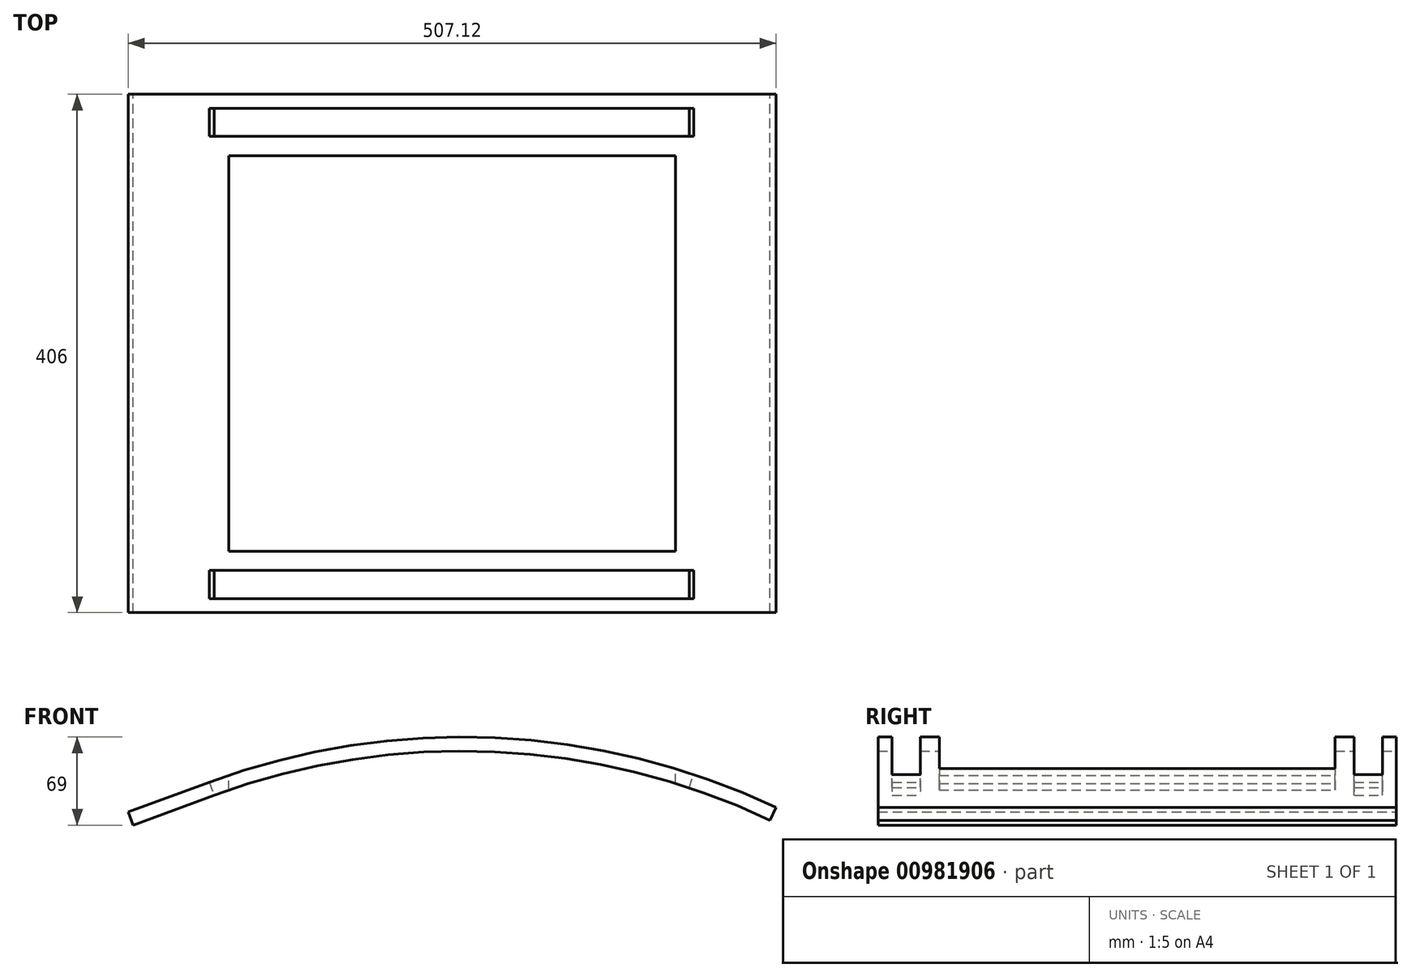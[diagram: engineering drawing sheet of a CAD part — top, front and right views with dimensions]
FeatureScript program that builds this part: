
annotation { "Feature Type Name" : "Feature", "Feature Type Description" : "" }
export const myFeature = defineFeature(function(context is Context, id is Id, definition is map)
    precondition{}
    {
        {
            var Q0;
            Q0=qCreatedBy(makeId("Front.planeOp"),FACE);
            var sketch = newSketch(context, id + "F0", { "sketchPlane" : qUnion([Q0])});
            skArc(sketch, "E0", {"start": v(249.02, -30.69) * mm, "mid": v(33.29, 22.94) * mm, "end": v(-186.38, -11.17) * mm});
            skArc(sketch, "E1", {"start": v(253.56, -20.66) * mm, "mid": v(33.68, 33.93) * mm, "end": v(-190.19, -0.84) * mm});
            skLineSegment(sketch, "E2", {"start": v(-249.76, -34.5) * mm, "end": v(-186.38, -11.17) * mm});
            skLineSegment(sketch, "E3", {"start": v(-253.56, -24.18) * mm, "end": v(-190.19, -0.84) * mm});
            skLineSegment(sketch, "E4", {"start": v(-249.76, -34.5) * mm, "end": v(-253.56, -24.18) * mm});
            skLineSegment(sketch, "E5", {"start": v(253.56, -20.66) * mm, "end": v(249.02, -30.69) * mm});
            skSolve(sketch);
        }
        {
            var Q0;
            Q0=makeQuery(id+"F0.imprint","IMPRINT",FACE,{"disambiguationData":[TD([[makeQuery(id+"F0.imprint","IMPRINT",EDGE,{"derivedFrom":sQuery(id+"F0.wireOp",EDGE,"E0")}),-1.0]])]});
            extrude(context, id + "F1", {"entities" : qUnion([Q0]), "depth" : 406 * mm, "offsetDistance" : 25 * mm});
        }
        {
            var Q0;
            Q0=makeQuery(id+"F1.opExtrude","CAP_FACE",FACE,{"disambiguationData":[OSD([sQuery(id+"F0.wireOp",EDGE,"E0"),sQuery(id+"F0.wireOp",EDGE,"E1"),sQuery(id+"F0.wireOp",EDGE,"E2"),sQuery(id+"F0.wireOp",EDGE,"E3"),sQuery(id+"F0.wireOp",EDGE,"E4"),sQuery(id+"F0.wireOp",EDGE,"E5")])],"isStart":false});
            cPlane(context, id + "F2", {"entities" : qUnion([Q0]), "cplaneType" : CPlaneType.OFFSET, "offset" : 11 * mm, "oppositeDirection" : true, "width" : 150 * mm, "height" : 150 * mm});
        }
        {
            var Q0;
            Q0=qCreatedBy(id+"F2.planeOp",FACE);
            var sketch = newSketch(context, id + "F3", { "sketchPlane" : qUnion([Q0])});
            skArc(sketch, "E6.0", {"start": v(190.64, 9.95) * mm, "mid": v(-1.15, 39.43) * mm, "end": v(-191.91, 3.85) * mm});
            skArc(sketch, "E7.0", {"start": v(184.02, -9.97) * mm, "mid": v(-0.82, 18.43) * mm, "end": v(-184.66, -15.86) * mm});
            skLineSegment(sketch, "E8", {"start": v(-191.91, 3.85) * mm, "end": v(-184.66, -15.86) * mm});
            skLineSegment(sketch, "E9", {"start": v(184.02, -9.97) * mm, "end": v(190.64, 9.95) * mm});
            skSolve(sketch);
        }
        {
            var Q0;
            Q0=makeQuery(id+"F3.imprint","IMPRINT",FACE,{"disambiguationData":[TD([[makeQuery(id+"F3.imprint","IMPRINT",EDGE,{"derivedFrom":sQuery(id+"F3.wireOp",EDGE,"E6.0")}),1.0]])]});
            extrude(context, id + "F4", {"entities" : qUnion([Q0]), "operationType" : NewBodyOperationType.REMOVE, "oppositeDirection" : true, "depth" : 22 * mm, "offsetDistance" : 25 * mm});
        }
        {
            var Q0;
            Q0=makeQuery(id+"F1.opExtrude","CAP_FACE",FACE,{"disambiguationData":[OSD([sQuery(id+"F0.wireOp",EDGE,"E0"),sQuery(id+"F0.wireOp",EDGE,"E1"),sQuery(id+"F0.wireOp",EDGE,"E2"),sQuery(id+"F0.wireOp",EDGE,"E3"),sQuery(id+"F0.wireOp",EDGE,"E4"),sQuery(id+"F0.wireOp",EDGE,"E5")])],"isStart":true});
            cPlane(context, id + "F5", {"entities" : qUnion([Q0]), "cplaneType" : CPlaneType.OFFSET, "offset" : 11 * mm, "oppositeDirection" : true, "width" : 150 * mm, "height" : 150 * mm});
        }
        {
            var Q0;
            Q0=qCreatedBy(id+"F5.planeOp",FACE);
            var sketch = newSketch(context, id + "F6", { "sketchPlane" : qUnion([Q0])});
            skArc(sketch, "E10.0", {"start": v(-190.64, 9.95) * mm, "mid": v(1.15, 39.43) * mm, "end": v(191.91, 3.85) * mm});
            skArc(sketch, "E10.1", {"start": v(-184.02, -9.97) * mm, "mid": v(0.82, 18.43) * mm, "end": v(184.66, -15.86) * mm});
            skLineSegment(sketch, "E10.2", {"start": v(191.91, 3.85) * mm, "end": v(184.66, -15.86) * mm});
            skLineSegment(sketch, "E10.3", {"start": v(-184.02, -9.97) * mm, "end": v(-190.64, 9.95) * mm});
            skSolve(sketch);
        }
        {
            var Q0;
            Q0 = qSketchRegion(id + "F6", true);
            extrude(context, id + "F7", {"entities" : qUnion([Q0]), "operationType" : NewBodyOperationType.REMOVE, "oppositeDirection" : true, "depth" : 22 * mm, "offsetDistance" : 25 * mm});
        }
        {
            var Q0;
            Q0=qCreatedBy(makeId("Top.planeOp"),FACE);
            cPlane(context, id + "F8", {"entities" : qUnion([Q0]), "cplaneType" : CPlaneType.OFFSET, "offset" : 134 * mm, "width" : 150 * mm, "height" : 150 * mm});
        }
        {
            var Q0;
            Q0=qCreatedBy(id+"F8.planeOp",FACE);
            var sketch = newSketch(context, id + "F9", { "sketchPlane" : qUnion([Q0])});
            skLineSegment(sketch, "E11.bottom", {"start": v(-175, -48) * mm, "end": v(175, -48) * mm});
            skLineSegment(sketch, "E11.top", {"start": v(-175, -358) * mm, "end": v(175, -358) * mm});
            skLineSegment(sketch, "E11.left", {"start": v(-175, -48) * mm, "end": v(-175, -358) * mm});
            skLineSegment(sketch, "E11.right", {"start": v(175, -48) * mm, "end": v(175, -358) * mm});
            skLineSegment(sketch, "E12.0", {"start": v(253.56, -406) * mm, "end": v(253.56, 0) * mm, "construction": true});
            skLineSegment(sketch, "E13", {"start": v(175, -203) * mm, "end": v(-175, -203) * mm, "construction": true});
            skPoint(sketch, "E14.orphan", {"position": v(253.56, -203) * mm});
            skLineSegment(sketch, "E15.0", {"start": v(-253.56, -406) * mm, "end": v(-253.56, 0) * mm, "construction": true});
            skLineSegment(sketch, "E16", {"start": v(-253.56, -406) * mm, "end": v(253.56, -406) * mm, "construction": true});
            skLineSegment(sketch, "E17", {"start": v(0, -406) * mm, "end": v(0, -449.72) * mm, "construction": true});
            skSolve(sketch);
        }
        {
            var Q0;
            Q0=makeQuery(id+"F9.imprint","IMPRINT",FACE,{"disambiguationData":[TD([[makeQuery(id+"F9.imprint","IMPRINT",EDGE,{"derivedFrom":sQuery(id+"F9.wireOp",EDGE,"E11.bottom")}),-1.0]])]});
            extrude(context, id + "F10", {"entities" : qUnion([Q0]), "operationType" : NewBodyOperationType.REMOVE, "oppositeDirection" : true, "depth" : 200 * mm, "offsetDistance" : 25 * mm});
        }
    });
